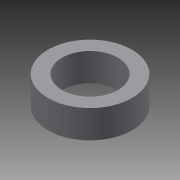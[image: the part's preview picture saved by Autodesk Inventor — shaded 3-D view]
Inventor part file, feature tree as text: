
AUTODESK INVENTOR PART (.ipt)
format: ipt  version: 2013 (Build 170138000, 138)  size: 73,216 bytes
history: native  units: in
note: dims shown in document units (in); Inventor stores cm internally (conversion verified against a paired STEP export)
features: extrude x1, sketch x1
ambient origin geometry x8: Origin, YZ Plane, XZ Plane, XY Plane, X Axis, Y Axis, Z Axis, Center Point
bodies: Solid1 (feature_tree)
feature tree (2):
  extrude  "Extrusion1"  Depth=0.75in
  sketch  "Sketch1"  dims[d0=0.5in d2=0.75in d3=0.25in d4=0.0in]
